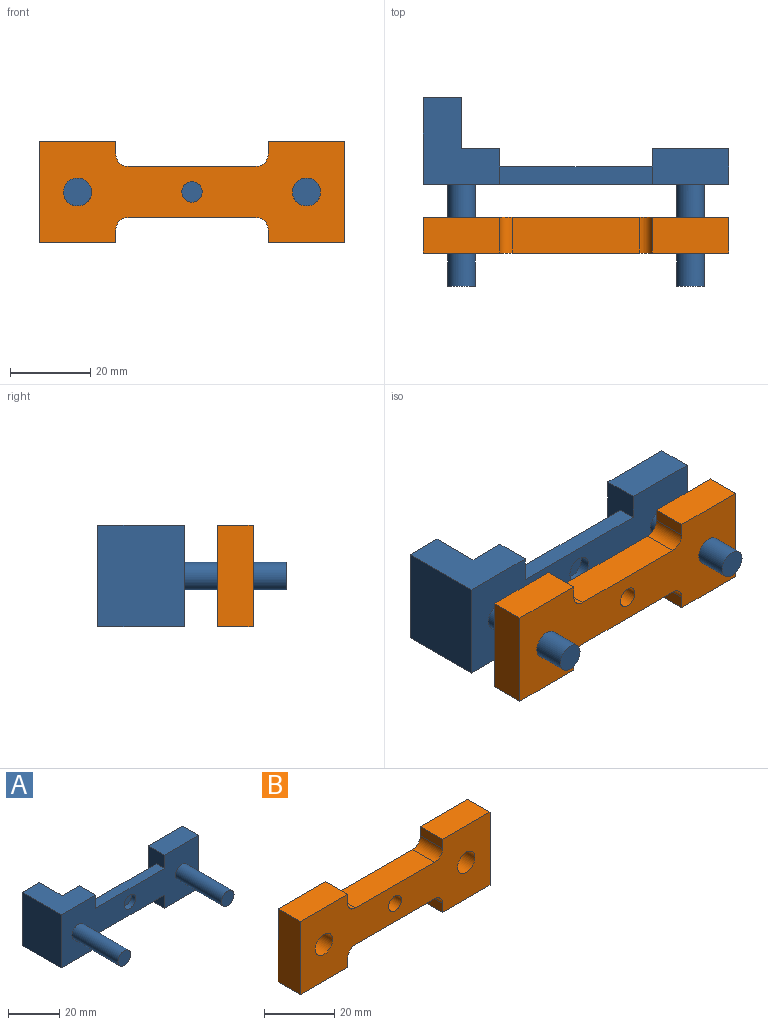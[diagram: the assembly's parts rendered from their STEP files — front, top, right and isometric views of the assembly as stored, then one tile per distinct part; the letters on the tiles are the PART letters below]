
ASSEMBLY  parts=2 mates=1
PART A: 24 faces, bbox 76.2x47x25.4 mm
  f0: plane 25.4x8.89mm, normal (-1,0,0), area 169.4mm2, adj f1,f3,f4,f5,f11,f12,f13
  f1: plane 76.2x25.4mm, normal (0,-1,0), area 1342mm2, adj f0,f2,f4,f5,f6,f7,f9,f10
  f2: plane 25.4x8.89mm, normal (1,0,0), area 225.8mm2, adj f1,f3,f4,f5
  f3: plane 25.4x19.05mm, normal (0,1,0), area 483.9mm2, adj f0,f2,f4,f5
  f4: plane 19.05x8.89mm, normal (0,0,1), area 169.4mm2, adj f0,f1,f2,f3
  f5: plane 19.05x8.89mm, normal (0,0,-1), area 169.4mm2, adj f0,f1,f2,f3
  f6: plane 25.4x8.89mm, normal (1,0,0), area 169.4mm2, adj f1,f8,f9,f10,f11,f12,f13
  f7: plane 25.4x21.59mm, normal (-1,0,0), area 548.4mm2, adj f1,f9,f10,f23
  f8: plane 25.4x12.7mm, normal (0,1,0), area 278.5mm2, adj f6,f9,f10,f20,f21,f22
  f9: plane 21.59x19.05mm, normal (0,0,1), area 290.3mm2, adj f1,f6,f7,f8,f20,f23
  f10: plane 21.59x19.05mm, normal (0,0,-1), area 290.3mm2, adj f1,f6,f7,f8,f22,f23
  f11: plane 38.1x12.7mm, normal (0,1,0), area 483.9mm2, adj f0,f6,f12,f13
  f12: plane 38.1x4.45mm, normal (0,0,1), area 169.4mm2, adj f0,f1,f6,f11
  f13: plane 38.1x4.45mm, normal (0,0,-1), area 169.4mm2, adj f0,f1,f6,f11
  f14: cylinder r=3.49mm len=25.4mm, axis (0,1,0), area 557.4mm2, adj f1,f15
  f15: plane 6.99x6.99mm, normal (0,-1,0), area 38.3mm2, adj f14
  f16: cylinder r=3.49mm len=25.4mm, axis (0,1,0), area 557.4mm2, adj f1,f17
  f17: plane 6.99x6.99mm, normal (0,-1,0), area 38.3mm2, adj f16
  f18: cylinder r=3.24mm len=6.48mm, axis (0,-1,0), area 51.7mm2, adj f1,f19
  f19: plane 6.48x6.48mm, normal (0,-1,0), area 32.9mm2, adj f18
  f20: plane 12.7x4.3mm, normal (1,0,0), area 54.6mm2, adj f8,f9,f21,f23
  f21: cylinder r=12.7mm len=16.8mm, axis (0,-1,0), area 233.1mm2, adj f8,f20,f22,f23
  f22: plane 12.7x4.3mm, normal (1,0,0), area 54.6mm2, adj f8,f10,f21,f23
  f23: plane 25.4x9.53mm, normal (0,1,0), area 205.4mm2, adj f7,f9,f10,f20,f21,f22
PART B: 21 faces, bbox 76.2x8.9x25.4 mm
  f0: plane 8.89x3.18mm, normal (-1,0,0), area 28.2mm2, adj f2,f4,f6,f16
  f1: plane 25.4x8.89mm, normal (1,0,0), area 225.8mm2, adj f2,f4,f5,f6
  f2: plane 76.2x25.4mm, normal (0,1,0), area 1363.2mm2, adj f0,f1,f3,f5,f6,f7,f8,f9
  f3: plane 8.89x3.18mm, normal (-1,0,0), area 28.2mm2, adj f2,f4,f5,f18
  f4: plane 76.2x25.4mm, normal (0,-1,0), area 1363.2mm2, adj f0,f1,f3,f5,f6,f7,f8,f9
  f5: plane 19.05x8.89mm, normal (0,0,1), area 169.4mm2, adj f1,f2,f3,f4
  f6: plane 19.05x8.89mm, normal (0,0,-1), area 169.4mm2, adj f0,f1,f2,f4
  f7: plane 8.89x3.18mm, normal (1,0,0), area 28.2mm2, adj f2,f4,f11,f17
  f8: plane 25.4x8.89mm, normal (-1,0,0), area 225.8mm2, adj f2,f4,f10,f11
  f9: plane 8.89x3.18mm, normal (1,0,0), area 28.2mm2, adj f2,f4,f10,f19
  f10: plane 19.05x8.89mm, normal (0,0,1), area 169.4mm2, adj f2,f4,f8,f9
  f11: plane 19.05x8.89mm, normal (0,0,-1), area 169.4mm2, adj f2,f4,f7,f8
  f12: plane 31.75x8.89mm, normal (0,0,1), area 282.3mm2, adj f2,f4,f18,f19
  f13: plane 31.75x8.89mm, normal (0,0,-1), area 282.3mm2, adj f2,f4,f16,f17
  f14: cylinder r=3.49mm len=8.89mm, axis (0,-1,0), area 195.1mm2, adj f2,f4
  f15: cylinder r=3.49mm len=8.89mm, axis (0,-1,0), area 195.1mm2, adj f2,f4
  f16: cylinder r=3.17mm len=8.89mm, axis (0,1,0), area 44.3mm2, adj f0,f2,f4,f13
  f17: cylinder r=3.17mm len=8.89mm, axis (0,-1,0), area 44.3mm2, adj f2,f4,f7,f13
  f18: cylinder r=3.17mm len=8.89mm, axis (0,-1,0), area 44.3mm2, adj f2,f3,f4,f12
  f19: cylinder r=3.17mm len=8.89mm, axis (0,1,0), area 44.3mm2, adj f2,f4,f9,f12
  f20: cylinder r=2.55mm len=8.89mm, axis (0,-1,0), area 142.6mm2, adj f2,f4
PLACE A t=(-16.88,23.78,-2.28)mm
PLACE B t=(-16.88,6.64,-2.28)mm
MATE slider A.f14 <-> B.f15  axis (0,1,0) through (-45.46,-7.97,-2.28)mm
